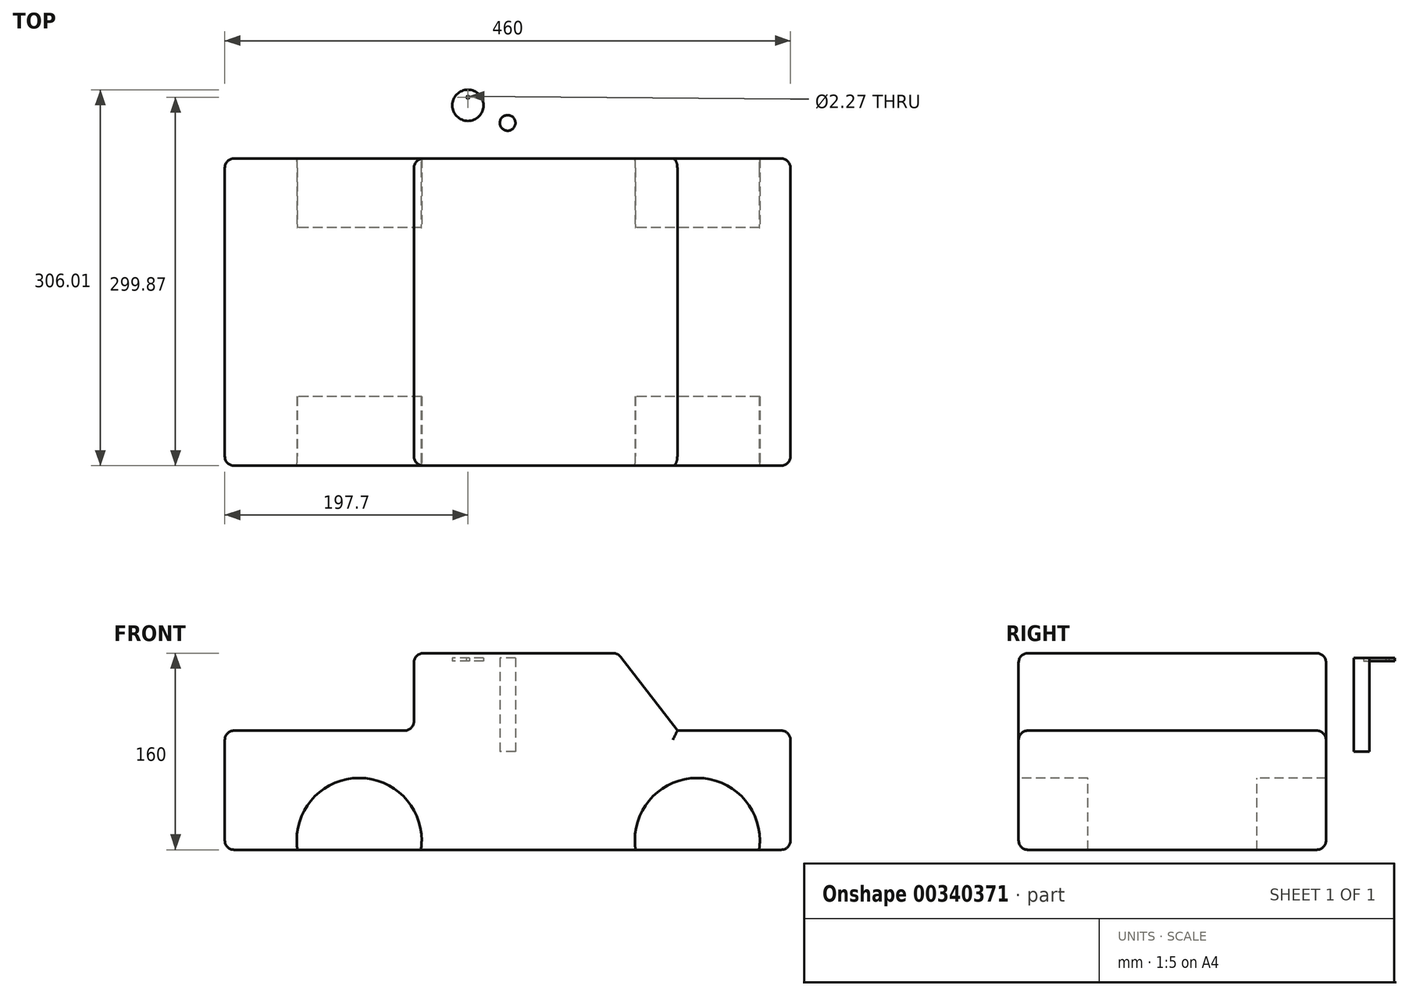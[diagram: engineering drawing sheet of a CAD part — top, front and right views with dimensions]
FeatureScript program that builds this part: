
annotation { "Feature Type Name" : "Feature", "Feature Type Description" : "" }
export const myFeature = defineFeature(function(context is Context, id is Id, definition is map)
    precondition{}
    {
        {
            var Q0;
            Q0=qCreatedBy(makeId("Front.planeOp"),FACE);
            var sketch = newSketch(context, id + "F0", { "sketchPlane" : qUnion([Q0])});
            skLineSegment(sketch, "E0.top", {"start": v(-230, -80) * mm, "end": v(230, -80) * mm});
            skLineSegment(sketch, "E0.right", {"start": v(230, 80) * mm, "end": v(230, 80) * mm});
            skPoint(sketch, "E0.middle", {"position": v(0, 0) * mm});
            skLineSegment(sketch, "E1", {"start": v(230, 17) * mm, "end": v(138.02, 17) * mm});
            skPoint(sketch, "E1.endSnap0", {"position": v(230, 17) * mm});
            skLineSegment(sketch, "E2", {"start": v(138.02, 17) * mm, "end": v(89.51, 80) * mm});
            skPoint(sketch, "E3.endSnap0", {"position": v(-230, 0) * mm});
            skLineSegment(sketch, "E4", {"start": v(-76.18, 0) * mm, "end": v(-76.18, 0.68) * mm});
            skLineSegment(sketch, "E5", {"start": v(-76.18, 80) * mm, "end": v(89.51, 80) * mm});
            skPoint(sketch, "E0.left.start.orphan", {"position": v(-230, 80) * mm});
            skPoint(sketch, "E6.end.orphan", {"position": v(230, -80) * mm});
            skPoint(sketch, "E6.start.orphan", {"position": v(230, 0) * mm});
            skLineSegment(sketch, "E7", {"start": v(230, -80) * mm, "end": v(230, 17) * mm});
            skLineSegment(sketch, "E8", {"start": v(-76.18, 17) * mm, "end": v(-230, 17) * mm});
            skLineSegment(sketch, "E9", {"start": v(-76.18, 17) * mm, "end": v(-76.18, 80) * mm});
            skLineSegment(sketch, "E10", {"start": v(-230, 17) * mm, "end": v(-230, -80) * mm});
            skSolve(sketch);
        }
        {
            var Q0;
            Q0=makeQuery(id+"F0.imprint","IMPRINT",FACE,{"disambiguationData":[TD([[makeQuery(id+"F0.imprint","IMPRINT",EDGE,{"derivedFrom":sQuery(id+"F0.wireOp",EDGE,"E0.top")}),1.0]])]});
            extrude(context, id + "F1", {"entities" : qUnion([Q0]), "depth" : 250 * mm});
        }
        {
            var Q0;
            Q0=makeQuery(id+"F1.opExtrude","CAP_EDGE",EDGE,{"disambiguationData":[OSD([sQuery(id+"F0.wireOp",EDGE,"E1")])],"isStart":false});
            var Q1;
            Q1=makeQuery(id+"F1.opExtrude","SWEPT_EDGE",EDGE,{"disambiguationData":[OSD([sQuery(id+"F0.wireOp",EDGE,"E1"),sQuery(id+"F0.wireOp",EDGE,"E7")])]});
            var Q2;
            Q2=makeQuery(id+"F1.opExtrude","CAP_EDGE",EDGE,{"disambiguationData":[OSD([sQuery(id+"F0.wireOp",EDGE,"E7")])],"isStart":false});
            var Q3;
            Q3=makeQuery(id+"F1.opExtrude","CAP_EDGE",EDGE,{"disambiguationData":[OSD([sQuery(id+"F0.wireOp",EDGE,"E2")])],"isStart":false});
            var Q4;
            Q4=makeQuery(id+"F1.opExtrude","SWEPT_EDGE",EDGE,{"disambiguationData":[OSD([sQuery(id+"F0.wireOp",EDGE,"E2"),sQuery(id+"F0.wireOp",EDGE,"E5")])]});
            var Q5;
            Q5=makeQuery(id+"F1.opExtrude","CAP_EDGE",EDGE,{"disambiguationData":[OSD([sQuery(id+"F0.wireOp",EDGE,"E1")])],"isStart":true});
            var Q6;
            Q6=makeQuery(id+"F1.opExtrude","CAP_EDGE",EDGE,{"disambiguationData":[OSD([sQuery(id+"F0.wireOp",EDGE,"E2")])],"isStart":true});
            var Q7;
            Q7=makeQuery(id+"F1.opExtrude","CAP_EDGE",EDGE,{"disambiguationData":[OSD([sQuery(id+"F0.wireOp",EDGE,"E7")])],"isStart":true});
            var Q8;
            Q8=makeQuery(id+"F1.opExtrude","SWEPT_EDGE",EDGE,{"disambiguationData":[OSD([sQuery(id+"F0.wireOp",EDGE,"E0.top"),sQuery(id+"F0.wireOp",EDGE,"E7")])]});
            var Q9;
            Q9=makeQuery(id+"F1.opExtrude","CAP_EDGE",EDGE,{"disambiguationData":[OSD([sQuery(id+"F0.wireOp",EDGE,"E0.top")])],"isStart":false});
            var Q10;
            Q10=makeQuery(id+"F1.opExtrude","CAP_FACE",FACE,{"disambiguationData":[OSD([sQuery(id+"F0.wireOp",EDGE,"E0.top"),sQuery(id+"F0.wireOp",EDGE,"E1"),sQuery(id+"F0.wireOp",EDGE,"E2"),sQuery(id+"F0.wireOp",EDGE,"E5"),sQuery(id+"F0.wireOp",EDGE,"E7"),sQuery(id+"F0.wireOp",EDGE,"E8"),sQuery(id+"F0.wireOp",EDGE,"E9"),sQuery(id+"F0.wireOp",EDGE,"E10")])],"isStart":false});
            var Q11;
            Q11=makeQuery(id+"F1.opExtrude","SWEPT_FACE",FACE,{"disambiguationData":[OSD([sQuery(id+"F0.wireOp",EDGE,"E9")])]});
            var Q12;
            Q12=makeQuery(id+"F1.opExtrude","SWEPT_FACE",FACE,{"disambiguationData":[OSD([sQuery(id+"F0.wireOp",EDGE,"E10")])]});
            var Q13;
            Q13=makeQuery(id+"F1.opExtrude","CAP_FACE",FACE,{"disambiguationData":[OSD([sQuery(id+"F0.wireOp",EDGE,"E0.top"),sQuery(id+"F0.wireOp",EDGE,"E1"),sQuery(id+"F0.wireOp",EDGE,"E2"),sQuery(id+"F0.wireOp",EDGE,"E5"),sQuery(id+"F0.wireOp",EDGE,"E7"),sQuery(id+"F0.wireOp",EDGE,"E8"),sQuery(id+"F0.wireOp",EDGE,"E9"),sQuery(id+"F0.wireOp",EDGE,"E10")])],"isStart":true});
            fillet(context, id + "F2", {"entities" : qUnion([Q0, Q1, Q2, Q3, Q4, Q5, Q6, Q7, Q8, Q9, Q10, Q11, Q12, Q13]), "radius" : 7.62 * mm, "tangentPropagation" : true, "allowEdgeOverflow" : false});
        }
        {
            var Q0;
            Q0=makeQuery(id+"F1.opExtrude","CAP_FACE",FACE,{"disambiguationData":[OSD([sQuery(id+"F0.wireOp",EDGE,"E0.top"),sQuery(id+"F0.wireOp",EDGE,"E1"),sQuery(id+"F0.wireOp",EDGE,"E2"),sQuery(id+"F0.wireOp",EDGE,"E5"),sQuery(id+"F0.wireOp",EDGE,"E7"),sQuery(id+"F0.wireOp",EDGE,"E8"),sQuery(id+"F0.wireOp",EDGE,"E9"),sQuery(id+"F0.wireOp",EDGE,"E10")])],"isStart":false});
            var sketch = newSketch(context, id + "F3", { "sketchPlane" : qUnion([Q0])});
            skCircle(sketch, "E11", {"center": v(154.25, -72.38) * mm, "radius": 50.8 * mm});
            skCircle(sketch, "E12", {"center": v(-120.75, -72.38) * mm, "radius": 50.8 * mm});
            skSolve(sketch);
        }
        {
            var Q0;
            {var subQ0=sQuery(id+"F3.wireOp",EDGE,"E12");var subQ1=sQuery(id+"F0.wireOp",EDGE,"E0.top");var subQ2=makeQuery(id+"F2.opFillet","BLEND_EDGE",EDGE,{"blendedFrom":[makeQuery(id+"F1.opExtrude","CAP_EDGE",EDGE,{"disambiguationData":[OSD([subQ1])],"isStart":false}),makeQuery(id+"F1.opExtrude","CAP_FACE",FACE,{"disambiguationData":[OSD([subQ1,sQuery(id+"F0.wireOp",EDGE,"E1"),sQuery(id+"F0.wireOp",EDGE,"E2"),sQuery(id+"F0.wireOp",EDGE,"E5"),sQuery(id+"F0.wireOp",EDGE,"E7"),sQuery(id+"F0.wireOp",EDGE,"E8"),sQuery(id+"F0.wireOp",EDGE,"E9"),sQuery(id+"F0.wireOp",EDGE,"E10")])],"isStart":false})],"blendedInto":[makeQuery(id+"F1.opExtrude","CAP_FACE",FACE,{"disambiguationData":[OSD([subQ1,sQuery(id+"F0.wireOp",EDGE,"E1"),sQuery(id+"F0.wireOp",EDGE,"E2"),sQuery(id+"F0.wireOp",EDGE,"E5"),sQuery(id+"F0.wireOp",EDGE,"E7"),sQuery(id+"F0.wireOp",EDGE,"E8"),sQuery(id+"F0.wireOp",EDGE,"E9"),sQuery(id+"F0.wireOp",EDGE,"E10")])],"isStart":false})]});var subQ3=makeQuery(id+"F3.imprint","INTERSECT",VERTEX,{"disambiguationData":[OD(0.0)],"derivedFrom":[subQ2,subQ0]});Q0=makeQuery(id+"F3.imprint","IMPRINT",FACE,{"disambiguationData":[TD([[makeQuery(id+"F3.imprint","IMPRINT",EDGE,{"disambiguationData":[TD([[subQ3,1.0]])],"derivedFrom":subQ0}),1.0]])]});}
            var Q1;
            {var subQ0=sQuery(id+"F3.wireOp",EDGE,"E12");var subQ1=sQuery(id+"F0.wireOp",EDGE,"E0.top");var subQ2=makeQuery(id+"F2.opFillet","BLEND_EDGE",EDGE,{"blendedFrom":[makeQuery(id+"F1.opExtrude","CAP_EDGE",EDGE,{"disambiguationData":[OSD([subQ1])],"isStart":false}),makeQuery(id+"F1.opExtrude","CAP_FACE",FACE,{"disambiguationData":[OSD([subQ1,sQuery(id+"F0.wireOp",EDGE,"E1"),sQuery(id+"F0.wireOp",EDGE,"E2"),sQuery(id+"F0.wireOp",EDGE,"E5"),sQuery(id+"F0.wireOp",EDGE,"E7"),sQuery(id+"F0.wireOp",EDGE,"E8"),sQuery(id+"F0.wireOp",EDGE,"E9"),sQuery(id+"F0.wireOp",EDGE,"E10")])],"isStart":false})],"blendedInto":[makeQuery(id+"F1.opExtrude","CAP_FACE",FACE,{"disambiguationData":[OSD([subQ1,sQuery(id+"F0.wireOp",EDGE,"E1"),sQuery(id+"F0.wireOp",EDGE,"E2"),sQuery(id+"F0.wireOp",EDGE,"E5"),sQuery(id+"F0.wireOp",EDGE,"E7"),sQuery(id+"F0.wireOp",EDGE,"E8"),sQuery(id+"F0.wireOp",EDGE,"E9"),sQuery(id+"F0.wireOp",EDGE,"E10")])],"isStart":false})]});var subQ3=makeQuery(id+"F3.imprint","INTERSECT",VERTEX,{"disambiguationData":[OD(0.0)],"derivedFrom":[subQ2,subQ0]});Q1=makeQuery(id+"F3.imprint","IMPRINT",FACE,{"disambiguationData":[TD([[makeQuery(id+"F3.imprint","IMPRINT",EDGE,{"disambiguationData":[TD([[subQ3,-1.0]])],"derivedFrom":subQ0}),1.0]])]});}
            var Q2;
            {var subQ0=sQuery(id+"F3.wireOp",EDGE,"E11");var subQ1=sQuery(id+"F0.wireOp",EDGE,"E0.top");var subQ2=makeQuery(id+"F2.opFillet","BLEND_EDGE",EDGE,{"blendedFrom":[makeQuery(id+"F1.opExtrude","CAP_EDGE",EDGE,{"disambiguationData":[OSD([subQ1])],"isStart":false}),makeQuery(id+"F1.opExtrude","CAP_FACE",FACE,{"disambiguationData":[OSD([subQ1,sQuery(id+"F0.wireOp",EDGE,"E1"),sQuery(id+"F0.wireOp",EDGE,"E2"),sQuery(id+"F0.wireOp",EDGE,"E5"),sQuery(id+"F0.wireOp",EDGE,"E7"),sQuery(id+"F0.wireOp",EDGE,"E8"),sQuery(id+"F0.wireOp",EDGE,"E9"),sQuery(id+"F0.wireOp",EDGE,"E10")])],"isStart":false})],"blendedInto":[makeQuery(id+"F1.opExtrude","CAP_FACE",FACE,{"disambiguationData":[OSD([subQ1,sQuery(id+"F0.wireOp",EDGE,"E1"),sQuery(id+"F0.wireOp",EDGE,"E2"),sQuery(id+"F0.wireOp",EDGE,"E5"),sQuery(id+"F0.wireOp",EDGE,"E7"),sQuery(id+"F0.wireOp",EDGE,"E8"),sQuery(id+"F0.wireOp",EDGE,"E9"),sQuery(id+"F0.wireOp",EDGE,"E10")])],"isStart":false})]});var subQ3=makeQuery(id+"F3.imprint","INTERSECT",VERTEX,{"disambiguationData":[OD(0.0)],"derivedFrom":[subQ2,subQ0]});Q2=makeQuery(id+"F3.imprint","IMPRINT",FACE,{"disambiguationData":[TD([[makeQuery(id+"F3.imprint","IMPRINT",EDGE,{"disambiguationData":[TD([[subQ3,-1.0]])],"derivedFrom":subQ0}),1.0]])]});}
            var Q3;
            {var subQ0=sQuery(id+"F3.wireOp",EDGE,"E11");var subQ1=sQuery(id+"F0.wireOp",EDGE,"E0.top");var subQ2=makeQuery(id+"F2.opFillet","BLEND_EDGE",EDGE,{"blendedFrom":[makeQuery(id+"F1.opExtrude","CAP_EDGE",EDGE,{"disambiguationData":[OSD([subQ1])],"isStart":false}),makeQuery(id+"F1.opExtrude","CAP_FACE",FACE,{"disambiguationData":[OSD([subQ1,sQuery(id+"F0.wireOp",EDGE,"E1"),sQuery(id+"F0.wireOp",EDGE,"E2"),sQuery(id+"F0.wireOp",EDGE,"E5"),sQuery(id+"F0.wireOp",EDGE,"E7"),sQuery(id+"F0.wireOp",EDGE,"E8"),sQuery(id+"F0.wireOp",EDGE,"E9"),sQuery(id+"F0.wireOp",EDGE,"E10")])],"isStart":false})],"blendedInto":[makeQuery(id+"F1.opExtrude","CAP_FACE",FACE,{"disambiguationData":[OSD([subQ1,sQuery(id+"F0.wireOp",EDGE,"E1"),sQuery(id+"F0.wireOp",EDGE,"E2"),sQuery(id+"F0.wireOp",EDGE,"E5"),sQuery(id+"F0.wireOp",EDGE,"E7"),sQuery(id+"F0.wireOp",EDGE,"E8"),sQuery(id+"F0.wireOp",EDGE,"E9"),sQuery(id+"F0.wireOp",EDGE,"E10")])],"isStart":false})]});var subQ3=makeQuery(id+"F3.imprint","INTERSECT",VERTEX,{"disambiguationData":[OD(0.0)],"derivedFrom":[subQ2,subQ0]});Q3=makeQuery(id+"F3.imprint","IMPRINT",FACE,{"disambiguationData":[TD([[makeQuery(id+"F3.imprint","IMPRINT",EDGE,{"disambiguationData":[TD([[subQ3,1.0]])],"derivedFrom":subQ0}),1.0]])]});}
            extrude(context, id + "F4", {"entities" : qUnion([Q0, Q1, Q2, Q3]), "operationType" : NewBodyOperationType.REMOVE, "oppositeDirection" : true, "depth" : 259.08 * mm});
        }
        {
            var Q0;
            {var subQ0=sQuery(id+"F0.wireOp",EDGE,"E0.top");Q0=makeQuery(id+"F4.boolean.opBoolean","SPLIT",FACE,{"disambiguationData":[TD([makeQuery(id+"F2.opFillet","BLEND_FACE",FACE,{"disambiguationData":[OSD([subQ0]),TDD([makeQuery(id+"F1.opExtrude","CAP_EDGE",EDGE,{"disambiguationData":[OSD([subQ0])],"isStart":true})])]}),makeQuery(id+"F2.opFillet","BLEND_FACE",FACE,{"disambiguationData":[OSD([subQ0]),TDD([makeQuery(id+"F1.opExtrude","CAP_EDGE",EDGE,{"disambiguationData":[OSD([subQ0])],"isStart":false})])]}),makeQuery(id+"F4.opExtrude","SWEPT_FACE",FACE,{"disambiguationData":[OSD([sQuery(id+"F3.wireOp",EDGE,"E11")])]}),makeQuery(id+"F4.opExtrude","SWEPT_FACE",FACE,{"disambiguationData":[OSD([sQuery(id+"F3.wireOp",EDGE,"E12")])]})])],"derivedFrom":makeQuery(id+"F1.opExtrude","SWEPT_FACE",FACE,{"disambiguationData":[OSD([subQ0])]})});}
            var sketch = newSketch(context, id + "F5", { "sketchPlane" : qUnion([Q0])});
            skLineSegment(sketch, "E13.bottom", {"start": v(213.76, 193.76) * mm, "end": v(-213.76, 193.76) * mm});
            skLineSegment(sketch, "E13.top", {"start": v(213.76, 56.24) * mm, "end": v(-213.76, 56.24) * mm});
            skLineSegment(sketch, "E13.left", {"start": v(213.76, 193.76) * mm, "end": v(213.76, 56.24) * mm});
            skLineSegment(sketch, "E13.right", {"start": v(-213.76, 193.76) * mm, "end": v(-213.76, 56.24) * mm});
            skPoint(sketch, "E13.middle", {"position": v(0, 125) * mm});
            skSolve(sketch);
        }
        {
            var Q0;
            {var subQ0=sQuery(id+"F5.wireOp",EDGE,"E13.right");Q0=makeQuery(id+"F5.imprint","IMPRINT",FACE,{"disambiguationData":[TD([[makeQuery(id+"F5.imprint","IMPRINT",EDGE,{"derivedFrom":subQ0}),1.0]])]});}
            var Q1;
            {var subQ0=sQuery(id+"F5.wireOp",EDGE,"E13.left");Q1=makeQuery(id+"F5.imprint","IMPRINT",FACE,{"disambiguationData":[TD([[makeQuery(id+"F5.imprint","IMPRINT",EDGE,{"derivedFrom":subQ0}),-1.0]])]});}
            var Q2;
            {var subQ0=sQuery(id+"F5.wireOp",EDGE,"E13.bottom");var subQ1=makeQuery(id+"F1.opExtrude","SWEPT_FACE",FACE,{"disambiguationData":[OSD([sQuery(id+"F0.wireOp",EDGE,"E0.top")])]});var subQ2=makeQuery(id+"F4.boolean.opBoolean","INTERSECT",EDGE,{"disambiguationData":[OD(1.0)],"derivedFrom":[subQ1,makeQuery(id+"F4.opExtrude","SWEPT_FACE",FACE,{"disambiguationData":[OSD([sQuery(id+"F3.wireOp",EDGE,"E11")])]})]});var subQ3=makeQuery(id+"F5.imprint","INTERSECT",VERTEX,{"derivedFrom":[subQ2,subQ0]});Q2=makeQuery(id+"F5.imprint","IMPRINT",FACE,{"disambiguationData":[TD([[makeQuery(id+"F5.imprint","IMPRINT",EDGE,{"disambiguationData":[TD([[subQ3,-1.0]])],"derivedFrom":subQ0}),1.0]])]});}
            extrude(context, id + "F6", {"entities" : qUnion([Q0, Q1, Q2]), "operationType" : NewBodyOperationType.ADD, "oppositeDirection" : true, "depth" : 88.9 * mm});
        }
        {
            var Q0;
            Q0=qCreatedBy(makeId("Top.planeOp"),FACE);
            var sketch = newSketch(context, id + "F7", { "sketchPlane" : qUnion([Q0])});
            skCircle(sketch, "E14", {"center": v(0, 29) * mm, "radius": 6.35 * mm});
            skCircle(sketch, "E15", {"center": v(-32.3, 43.3) * mm, "radius": 12.7 * mm});
            skCircle(sketch, "E16", {"center": v(-32.3, 49.87) * mm, "radius": 1.13 * mm});
            skSolve(sketch);
        }
        {
            var Q0;
            Q0 = qSketchRegion(id + "F7", true);
            extrude(context, id + "F8", {"entities" : qUnion([Q0]), "depth" : 76.2 * mm});
        }
        {
            var Q0;
            Q0=makeQuery(id+"F8.opExtrude","CAP_FACE",FACE,{"disambiguationData":[OSD([sQuery(id+"F7.wireOp",EDGE,"E15")])],"isStart":true});
            extrude(context, id + "F9", {"entities" : qUnion([Q0]), "operationType" : NewBodyOperationType.REMOVE, "oppositeDirection" : true, "depth" : 73.66 * mm});
        }
    });
